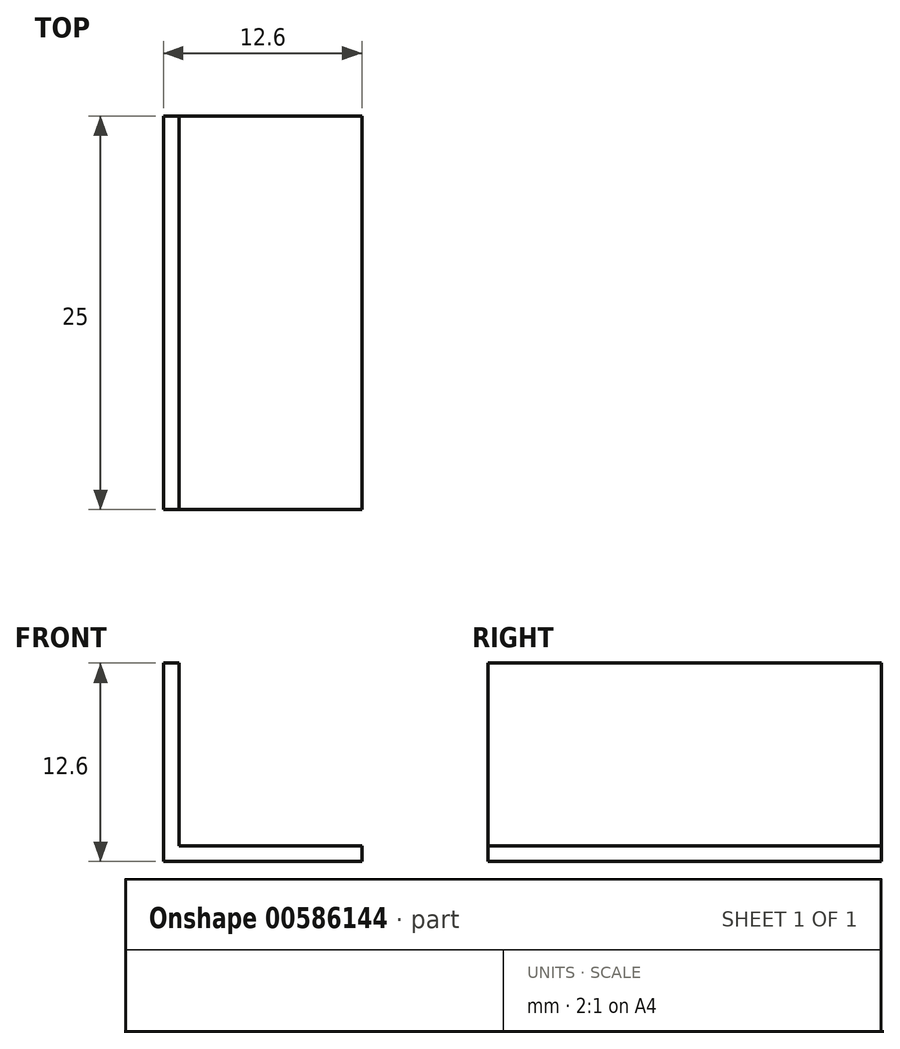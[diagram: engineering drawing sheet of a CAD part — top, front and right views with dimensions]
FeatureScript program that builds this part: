
annotation { "Feature Type Name" : "Feature", "Feature Type Description" : "" }
export const myFeature = defineFeature(function(context is Context, id is Id, definition is map)
    precondition{}
    {
        {
            var Q0;
            Q0=qCreatedBy(makeId("Front.planeOp"),FACE);
            var sketch = newSketch(context, id + "F0", { "sketchPlane" : qUnion([Q0])});
            skLineSegment(sketch, "E0", {"start": v(0, 0) * mm, "end": v(0, 12.6) * mm});
            skLineSegment(sketch, "E1", {"start": v(0, 0) * mm, "end": v(12.6, 0) * mm});
            skLineSegment(sketch, "E2", {"start": v(0, 12.6) * mm, "end": v(1, 12.6) * mm});
            skLineSegment(sketch, "E3", {"start": v(1, 12.6) * mm, "end": v(1, 1) * mm});
            skLineSegment(sketch, "E4", {"start": v(1, 1) * mm, "end": v(12.6, 1) * mm});
            skLineSegment(sketch, "E5", {"start": v(12.6, 1) * mm, "end": v(12.6, 0) * mm});
            skSolve(sketch);
        }
        {
            var Q0;
            Q0 = qSketchRegion(id + "F0", true);
            extrude(context, id + "F1", {"entities" : qUnion([Q0]), "depth" : 25 * mm, "offsetDistance" : 25 * mm});
        }
    });
